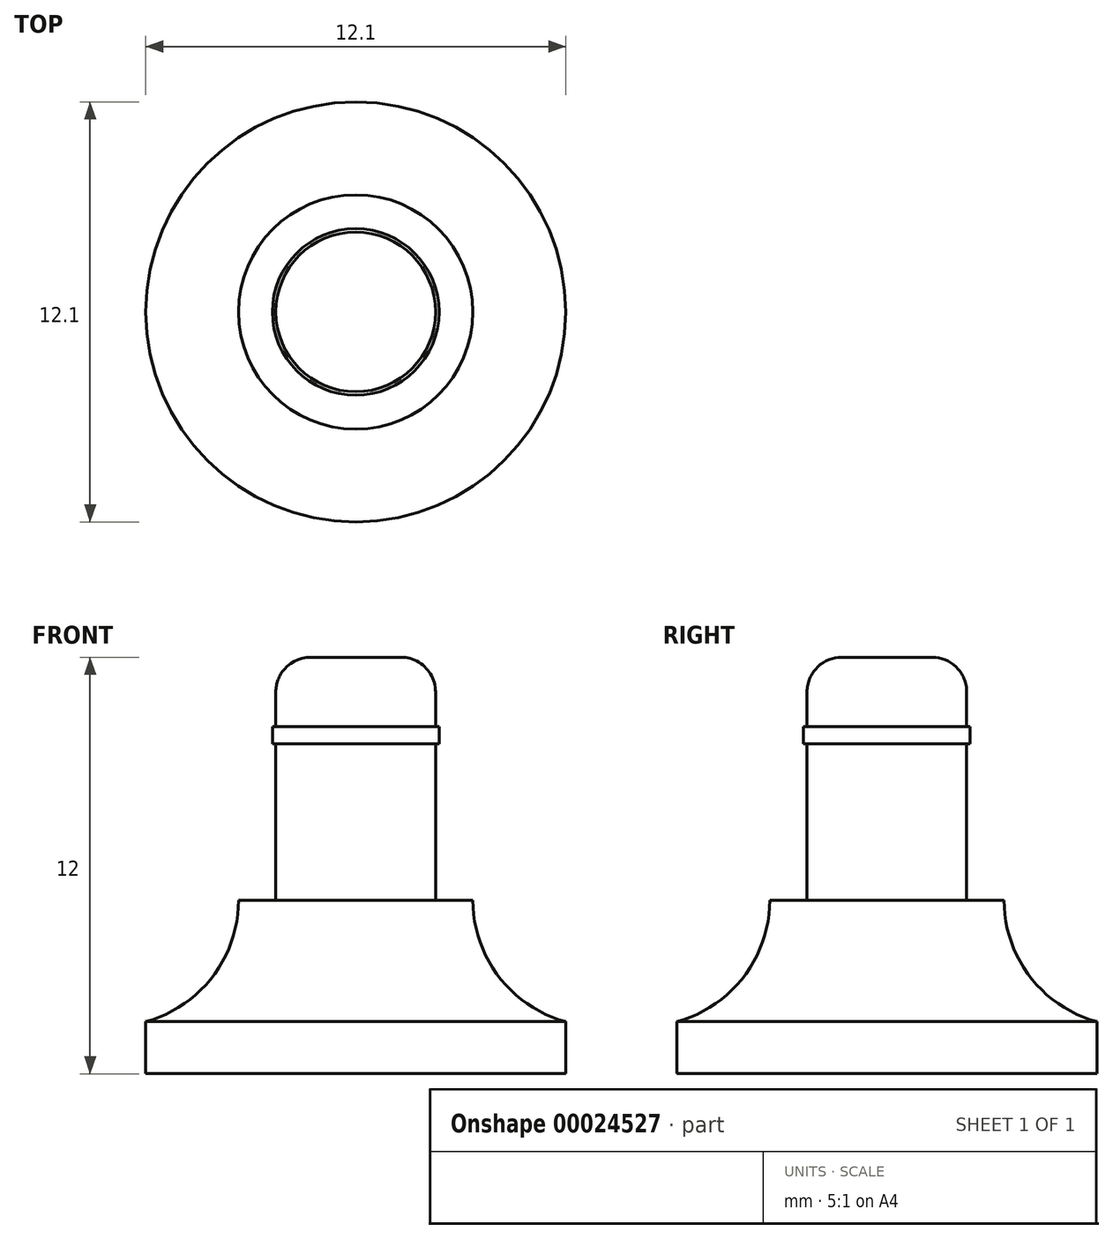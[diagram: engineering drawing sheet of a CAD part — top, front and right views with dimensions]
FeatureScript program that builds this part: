
annotation { "Feature Type Name" : "Feature", "Feature Type Description" : "" }
export const myFeature = defineFeature(function(context is Context, id is Id, definition is map)
    precondition{}
    {
        {
            var Q0;
            Q0=qCreatedBy(makeId("Front.planeOp"),FACE);
            var sketch = newSketch(context, id + "F0", { "sketchPlane" : qUnion([Q0])});
            skLineSegment(sketch, "E0", {"start": v(-24.2, 36.53) * mm, "end": v(-24.2, 24.53) * mm});
            skLineSegment(sketch, "E1", {"start": v(-24.2, 24.53) * mm, "end": v(-18.15, 24.53) * mm});
            skLineSegment(sketch, "E2", {"start": v(-18.15, 24.53) * mm, "end": v(-18.15, 26.03) * mm});
            skLineSegment(sketch, "E3", {"start": v(-24.2, 36.53) * mm, "end": v(-22.9, 36.53) * mm});
            skLineSegment(sketch, "E4", {"start": v(-21.9, 29.53) * mm, "end": v(-20.83, 29.53) * mm});
            skLineSegment(sketch, "E5", {"start": v(-21.9, 29.53) * mm, "end": v(-21.9, 34.03) * mm});
            skLineSegment(sketch, "E6", {"start": v(-21.9, 34.03) * mm, "end": v(-21.8, 34.03) * mm});
            skLineSegment(sketch, "E7", {"start": v(-21.9, 35.53) * mm, "end": v(-21.9, 34.53) * mm});
            skLineSegment(sketch, "E8", {"start": v(-21.9, 34.53) * mm, "end": v(-21.8, 34.53) * mm});
            skLineSegment(sketch, "E9", {"start": v(-21.8, 34.53) * mm, "end": v(-21.8, 34.03) * mm});
            skPoint(sketch, "E10.visualSharp", {"position": v(-21.9, 36.53) * mm});
            skArc(sketch, "E10.filletArc", {"start": v(-21.9, 35.53) * mm, "mid": v(-22.2, 36.24) * mm, "end": v(-22.9, 36.53) * mm});
            skArc(sketch, "E11", {"start": v(-20.83, 29.53) * mm, "mid": v(-20.08, 27.33) * mm, "end": v(-18.15, 26.03) * mm});
            skSolve(sketch);
        }
        {
            var Q0;
            Q0=makeQuery(id+"F0.imprint","IMPRINT",FACE,{"disambiguationData":[TD([[makeQuery(id+"F0.imprint","IMPRINT",EDGE,{"derivedFrom":sQuery(id+"F0.wireOp",EDGE,"E0")}),1.0]])]});
            var Q1;
            Q1=sQuery(id+"F0.wireOp",EDGE,"E0");
            revolve(context, id + "F1", {"entities" : qUnion([Q0]), "axis" : qUnion([Q1]), "revolveType" : RevolveType.FULL});
        }
    });
